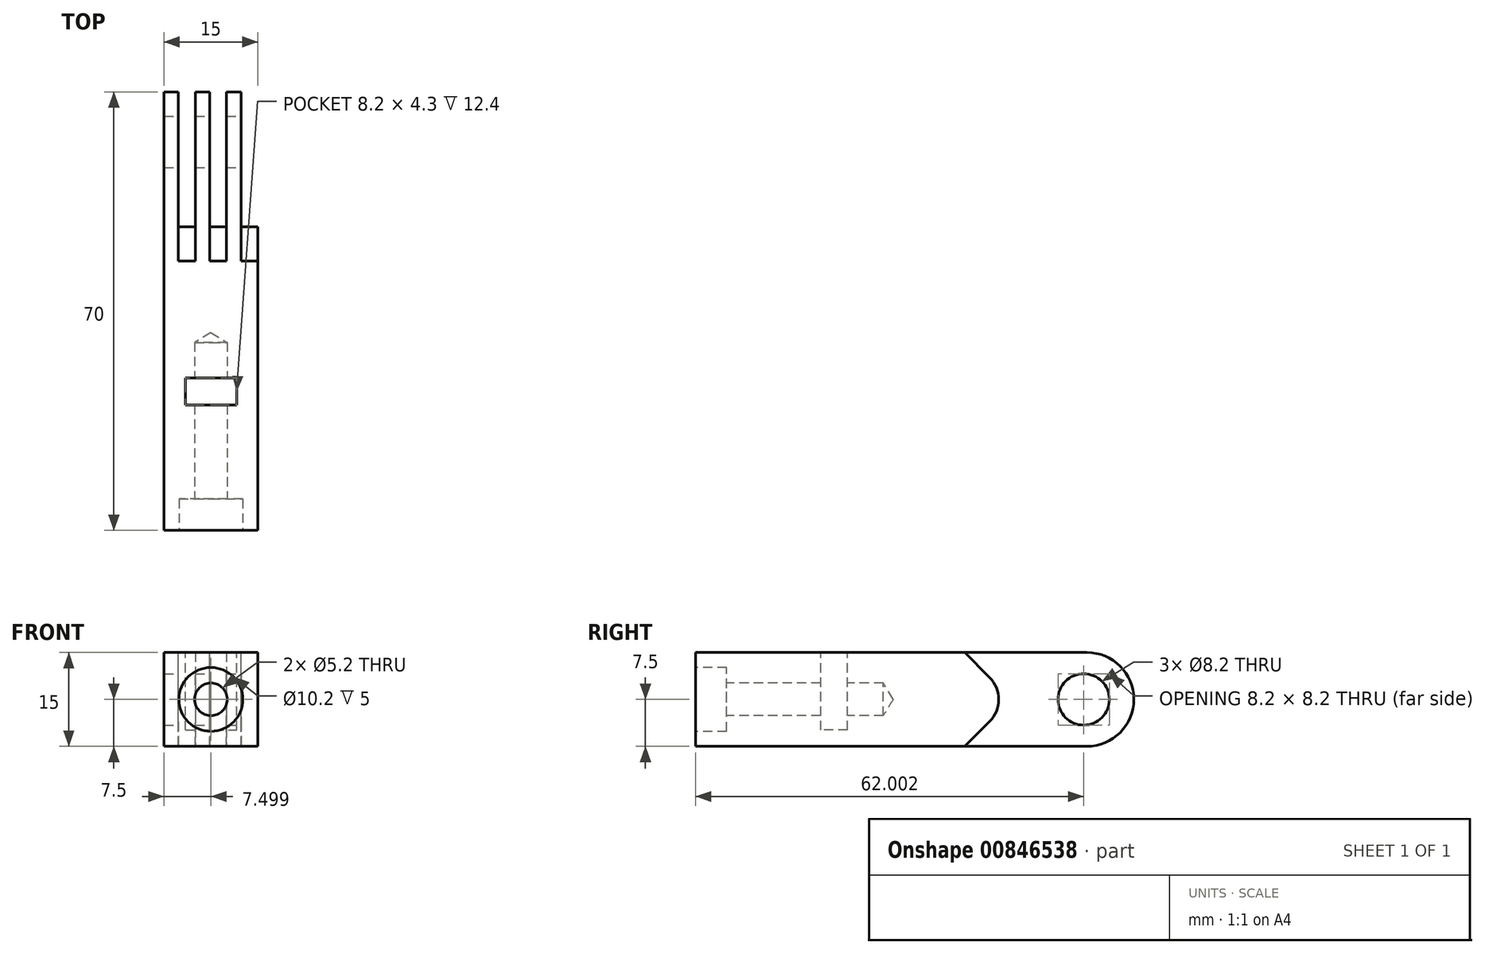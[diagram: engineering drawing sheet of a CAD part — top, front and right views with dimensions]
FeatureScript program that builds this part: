
annotation { "Feature Type Name" : "Feature", "Feature Type Description" : "" }
export const myFeature = defineFeature(function(context is Context, id is Id, definition is map)
    precondition{}
    {
        {
            var Q0;
            Q0=qCreatedBy(makeId("Top.planeOp"),FACE);
            var sketch = newSketch(context, id + "F0", { "sketchPlane" : qUnion([Q0])});
            skLineSegment(sketch, "E0", {"start": v(-7.04, -7.7) * mm, "end": v(-7.04, 62.3) * mm});
            skLineSegment(sketch, "E1", {"start": v(-7.04, 62.3) * mm, "end": v(-4.74, 62.3) * mm});
            skLineSegment(sketch, "E2", {"start": v(-4.74, 62.3) * mm, "end": v(-4.74, 46.3) * mm});
            skLineSegment(sketch, "E3", {"start": v(-4.74, 46.3) * mm, "end": v(-2.04, 46.3) * mm});
            skLineSegment(sketch, "E4", {"start": v(-2.04, 46.3) * mm, "end": v(-2.04, 62.3) * mm});
            skLineSegment(sketch, "E5", {"start": v(-2.04, 62.3) * mm, "end": v(0.26, 62.3) * mm});
            skLineSegment(sketch, "E6", {"start": v(0.26, 62.3) * mm, "end": v(0.26, 46.3) * mm});
            skLineSegment(sketch, "E7", {"start": v(0.26, 46.3) * mm, "end": v(2.96, 46.3) * mm});
            skLineSegment(sketch, "E8", {"start": v(2.96, 46.3) * mm, "end": v(2.96, 62.3) * mm});
            skLineSegment(sketch, "E9", {"start": v(2.96, 62.3) * mm, "end": v(5.26, 62.3) * mm});
            skLineSegment(sketch, "E10", {"start": v(5.26, 62.3) * mm, "end": v(5.26, 46.3) * mm});
            skLineSegment(sketch, "E11", {"start": v(5.26, 46.3) * mm, "end": v(7.96, 46.3) * mm});
            skLineSegment(sketch, "E12", {"start": v(7.96, 46.3) * mm, "end": v(7.96, -7.7) * mm});
            skLineSegment(sketch, "E13", {"start": v(7.96, -7.7) * mm, "end": v(-7.04, -7.7) * mm});
            skSolve(sketch);
        }
        {
            var Q0;
            Q0=makeQuery(id+"F0.imprint","IMPRINT",FACE,{"disambiguationData":[TD([[makeQuery(id+"F0.imprint","IMPRINT",EDGE,{"derivedFrom":sQuery(id+"F0.wireOp",EDGE,"E0")}),-1.0]])]});
            extrude(context, id + "F1", {"entities" : qUnion([Q0]), "depth" : 15 * mm, "offsetDistance" : 25 * mm});
        }
        {
            var Q0;
            Q0=makeQuery(id+"F1.opExtrude","SWEPT_FACE",FACE,{"disambiguationData":[OSD([sQuery(id+"F0.wireOp",EDGE,"E13")])]});
            var sketch = newSketch(context, id + "F2", { "sketchPlane" : qUnion([Q0])});
            skLineSegment(sketch, "E14.bottom", {"start": v(-7.04, 15) * mm, "end": v(7.96, 15) * mm});
            skLineSegment(sketch, "E14.top", {"start": v(-7.04, 0) * mm, "end": v(7.96, 0) * mm});
            skLineSegment(sketch, "E14.left", {"start": v(-7.04, 15) * mm, "end": v(-7.04, 0) * mm});
            skLineSegment(sketch, "E14.right", {"start": v(7.96, 15) * mm, "end": v(7.96, 0) * mm});
            skPoint(sketch, "E15", {"position": v(0.46, 7.5) * mm});
            skPoint(sketch, "E15.positionSnap0", {"position": v(7.96, 7.5) * mm});
            skPoint(sketch, "E15.positionSnap1", {"position": v(0.46, 15) * mm});
            skPoint(sketch, "E16", {"position": v(10.18, 9.66) * mm});
            skCircle(sketch, "E17", {"center": v(0.46, 7.5) * mm, "radius": 2.6 * mm});
            skSolve(sketch);
        }
        {
            var Q0;
            Q0=sQuery(id+"F2.wireOp",VERTEX,"E15");
            var Q1;
            Q1=makeQuery(id+"F1.opExtrude","SWEPT_BODY",BODY,{"disambiguationData":[OSD([sQuery(id+"F0.wireOp",EDGE,"E0"),sQuery(id+"F0.wireOp",EDGE,"E1"),sQuery(id+"F0.wireOp",EDGE,"E2"),sQuery(id+"F0.wireOp",EDGE,"E3"),sQuery(id+"F0.wireOp",EDGE,"E4"),sQuery(id+"F0.wireOp",EDGE,"E5"),sQuery(id+"F0.wireOp",EDGE,"E6"),sQuery(id+"F0.wireOp",EDGE,"E7"),sQuery(id+"F0.wireOp",EDGE,"E8"),sQuery(id+"F0.wireOp",EDGE,"E9"),sQuery(id+"F0.wireOp",EDGE,"E10"),sQuery(id+"F0.wireOp",EDGE,"E11"),sQuery(id+"F0.wireOp",EDGE,"E12"),sQuery(id+"F0.wireOp",EDGE,"E13")])]});
            hole(context, id + "F3", {"style" : HoleStyle.C_BORE, "endStyle" : HoleEndStyle.BLIND, "holeDiameter" : 5.2 * mm, "cBoreDiameter" : 10.2 * mm, "cBoreDepth" : 5 * mm, "majorDiameter" : 5 * mm, "holeDepth" : 30 * mm, "isTappedThrough" : true, "tappedDepth" : 12 * mm, "tapClearance" : 3, "locations" : qUnion([Q0]), "scope" : qUnion([Q1])});
        }
        {
            var Q0;
            Q0=makeQuery(id+"F1.opExtrude","CAP_FACE",FACE,{"disambiguationData":[OSD([sQuery(id+"F0.wireOp",EDGE,"E0"),sQuery(id+"F0.wireOp",EDGE,"E1"),sQuery(id+"F0.wireOp",EDGE,"E2"),sQuery(id+"F0.wireOp",EDGE,"E3"),sQuery(id+"F0.wireOp",EDGE,"E4"),sQuery(id+"F0.wireOp",EDGE,"E5"),sQuery(id+"F0.wireOp",EDGE,"E6"),sQuery(id+"F0.wireOp",EDGE,"E7"),sQuery(id+"F0.wireOp",EDGE,"E8"),sQuery(id+"F0.wireOp",EDGE,"E9"),sQuery(id+"F0.wireOp",EDGE,"E10"),sQuery(id+"F0.wireOp",EDGE,"E11"),sQuery(id+"F0.wireOp",EDGE,"E12"),sQuery(id+"F0.wireOp",EDGE,"E13")])],"isStart":false});
            var sketch = newSketch(context, id + "F4", { "sketchPlane" : qUnion([Q0])});
            skLineSegment(sketch, "E18.bottom", {"start": v(-7.04, -7.7) * mm, "end": v(7.96, -7.7) * mm});
            skLineSegment(sketch, "E18.top", {"start": v(-7.04, 37.3) * mm, "end": v(7.96, 37.3) * mm});
            skLineSegment(sketch, "E18.left", {"start": v(-7.04, -7.7) * mm, "end": v(-7.04, 37.3) * mm});
            skLineSegment(sketch, "E18.right", {"start": v(7.96, -7.7) * mm, "end": v(7.96, 37.3) * mm});
            skLineSegment(sketch, "E19.bottom", {"start": v(-3.64, 16.6) * mm, "end": v(4.56, 16.6) * mm});
            skLineSegment(sketch, "E19.top", {"start": v(-3.64, 12.3) * mm, "end": v(4.56, 12.3) * mm});
            skLineSegment(sketch, "E19.left", {"start": v(-3.64, 16.6) * mm, "end": v(-3.64, 12.3) * mm});
            skLineSegment(sketch, "E19.right", {"start": v(4.56, 16.6) * mm, "end": v(4.56, 12.3) * mm});
            skSolve(sketch);
        }
        {
            var Q0;
            Q0=makeQuery(id+"F4.imprint","IMPRINT",FACE,{"disambiguationData":[TD([[makeQuery(id+"F4.imprint","IMPRINT",EDGE,{"derivedFrom":sQuery(id+"F4.wireOp",EDGE,"E19.bottom")}),-1.0]])]});
            extrude(context, id + "F5", {"entities" : qUnion([Q0]), "operationType" : NewBodyOperationType.REMOVE, "oppositeDirection" : true, "depth" : 12.4 * mm, "offsetDistance" : 25 * mm});
        }
        {
            var Q0;
            Q0=makeQuery(id+"F1.opExtrude","SWEPT_FACE",FACE,{"disambiguationData":[OSD([sQuery(id+"F0.wireOp",EDGE,"E10")])]});
            var sketch = newSketch(context, id + "F6", { "sketchPlane" : qUnion([Q0])});
            skCircle(sketch, "E20", {"center": v(54.3, 7.5) * mm, "radius": 4.1 * mm});
            skPoint(sketch, "E20.centerSnap0", {"position": v(62.3, 7.5) * mm});
            skPoint(sketch, "E20.centerSnap1", {"position": v(54.3, 15) * mm});
            skSolve(sketch);
        }
        {
            var Q0;
            Q0=makeQuery(id+"F6.imprint","IMPRINT",FACE,{"disambiguationData":[TD([[makeQuery(id+"F6.imprint","IMPRINT",EDGE,{"derivedFrom":sQuery(id+"F6.wireOp",EDGE,"E20")}),1.0]])]});
            extrude(context, id + "F7", {"entities" : qUnion([Q0]), "operationType" : NewBodyOperationType.REMOVE, "oppositeDirection" : true, "depth" : 25 * mm, "offsetDistance" : 25 * mm});
        }
        {
            var Q0;
            Q0=makeQuery(id+"F1.opExtrude","CAP_EDGE",EDGE,{"disambiguationData":[OSD([sQuery(id+"F0.wireOp",EDGE,"E1")])],"isStart":true});
            fillet(context, id + "F8", {"entities" : qUnion([Q0]), "radius" : 7.5 * mm, "tangentPropagation" : true, "allowEdgeOverflow" : false});
        }
        {
            var Q0;
            Q0=makeQuery(id+"F1.opExtrude","CAP_EDGE",EDGE,{"disambiguationData":[OSD([sQuery(id+"F0.wireOp",EDGE,"E5")])],"isStart":true});
            var Q1;
            Q1=makeQuery(id+"F1.opExtrude","CAP_EDGE",EDGE,{"disambiguationData":[OSD([sQuery(id+"F0.wireOp",EDGE,"E9")])],"isStart":true});
            fillet(context, id + "F9", {"entities" : qUnion([Q0, Q1]), "radius" : 7.5 * mm, "tangentPropagation" : true, "allowEdgeOverflow" : false});
        }
        {
            var Q0;
            Q0=makeQuery(id+"F1.opExtrude","CAP_EDGE",EDGE,{"disambiguationData":[OSD([sQuery(id+"F0.wireOp",EDGE,"E1")])],"isStart":false});
            var Q1;
            Q1=makeQuery(id+"F1.opExtrude","CAP_EDGE",EDGE,{"disambiguationData":[OSD([sQuery(id+"F0.wireOp",EDGE,"E5")])],"isStart":false});
            var Q2;
            Q2=makeQuery(id+"F1.opExtrude","CAP_EDGE",EDGE,{"disambiguationData":[OSD([sQuery(id+"F0.wireOp",EDGE,"E9")])],"isStart":false});
            fillet(context, id + "F10", {"entities" : qUnion([Q0, Q1, Q2]), "radius" : 7.5 * mm, "tangentPropagation" : true, "allowEdgeOverflow" : false});
        }
        {
            var Q0;
            Q0=makeQuery(id+"F1.opExtrude","CAP_EDGE",EDGE,{"disambiguationData":[OSD([sQuery(id+"F0.wireOp",EDGE,"E3")])],"isStart":false});
            var Q1;
            Q1=makeQuery(id+"F1.opExtrude","CAP_EDGE",EDGE,{"disambiguationData":[OSD([sQuery(id+"F0.wireOp",EDGE,"E7")])],"isStart":false});
            var Q2;
            Q2=makeQuery(id+"F1.opExtrude","CAP_EDGE",EDGE,{"disambiguationData":[OSD([sQuery(id+"F0.wireOp",EDGE,"E11")])],"isStart":false});
            chamfer(context, id + "F11", {"entities" : qUnion([Q0, Q1, Q2]), "width" : 11 * mm, "tangentPropagation" : true});
        }
        {
            var Q0;
            Q0=makeQuery(id+"F1.opExtrude","CAP_EDGE",EDGE,{"disambiguationData":[OSD([sQuery(id+"F0.wireOp",EDGE,"E3")])],"isStart":true});
            var Q1;
            Q1=makeQuery(id+"F1.opExtrude","CAP_EDGE",EDGE,{"disambiguationData":[OSD([sQuery(id+"F0.wireOp",EDGE,"E7")])],"isStart":true});
            var Q2;
            Q2=makeQuery(id+"F1.opExtrude","CAP_EDGE",EDGE,{"disambiguationData":[OSD([sQuery(id+"F0.wireOp",EDGE,"E11")])],"isStart":true});
            chamfer(context, id + "F12", {"entities" : qUnion([Q0, Q1, Q2]), "width" : 11 * mm, "tangentPropagation" : true});
        }
        {
            var Q0;
            {var subQ0=sQuery(id+"F0.wireOp",EDGE,"E11");Q0=makeQuery(id+"F12.opChamfer","BLEND_EDGE",EDGE,{"blendedFrom":[makeQuery(id+"F1.opExtrude","CAP_EDGE",EDGE,{"disambiguationData":[OSD([subQ0])],"isStart":true}),makeQuery(id+"F11.opChamfer","BLEND_FACE",FACE,{"disambiguationData":[OSD([subQ0])]})],"blendedInto":[makeQuery(id+"F11.opChamfer","BLEND_FACE",FACE,{"disambiguationData":[OSD([subQ0])]})]});}
            var Q1;
            {var subQ0=sQuery(id+"F0.wireOp",EDGE,"E7");Q1=makeQuery(id+"F12.opChamfer","BLEND_EDGE",EDGE,{"blendedFrom":[makeQuery(id+"F1.opExtrude","CAP_EDGE",EDGE,{"disambiguationData":[OSD([subQ0])],"isStart":true}),makeQuery(id+"F11.opChamfer","BLEND_FACE",FACE,{"disambiguationData":[OSD([subQ0])]})],"blendedInto":[makeQuery(id+"F11.opChamfer","BLEND_FACE",FACE,{"disambiguationData":[OSD([subQ0])]})]});}
            var Q2;
            {var subQ0=sQuery(id+"F0.wireOp",EDGE,"E3");Q2=makeQuery(id+"F12.opChamfer","BLEND_EDGE",EDGE,{"blendedFrom":[makeQuery(id+"F1.opExtrude","CAP_EDGE",EDGE,{"disambiguationData":[OSD([subQ0])],"isStart":true}),makeQuery(id+"F11.opChamfer","BLEND_FACE",FACE,{"disambiguationData":[OSD([subQ0])]})],"blendedInto":[makeQuery(id+"F11.opChamfer","BLEND_FACE",FACE,{"disambiguationData":[OSD([subQ0])]})]});}
            fillet(context, id + "F13", {"entities" : qUnion([Q0, Q1, Q2]), "radius" : 5 * mm, "tangentPropagation" : true, "allowEdgeOverflow" : false});
        }
    });
